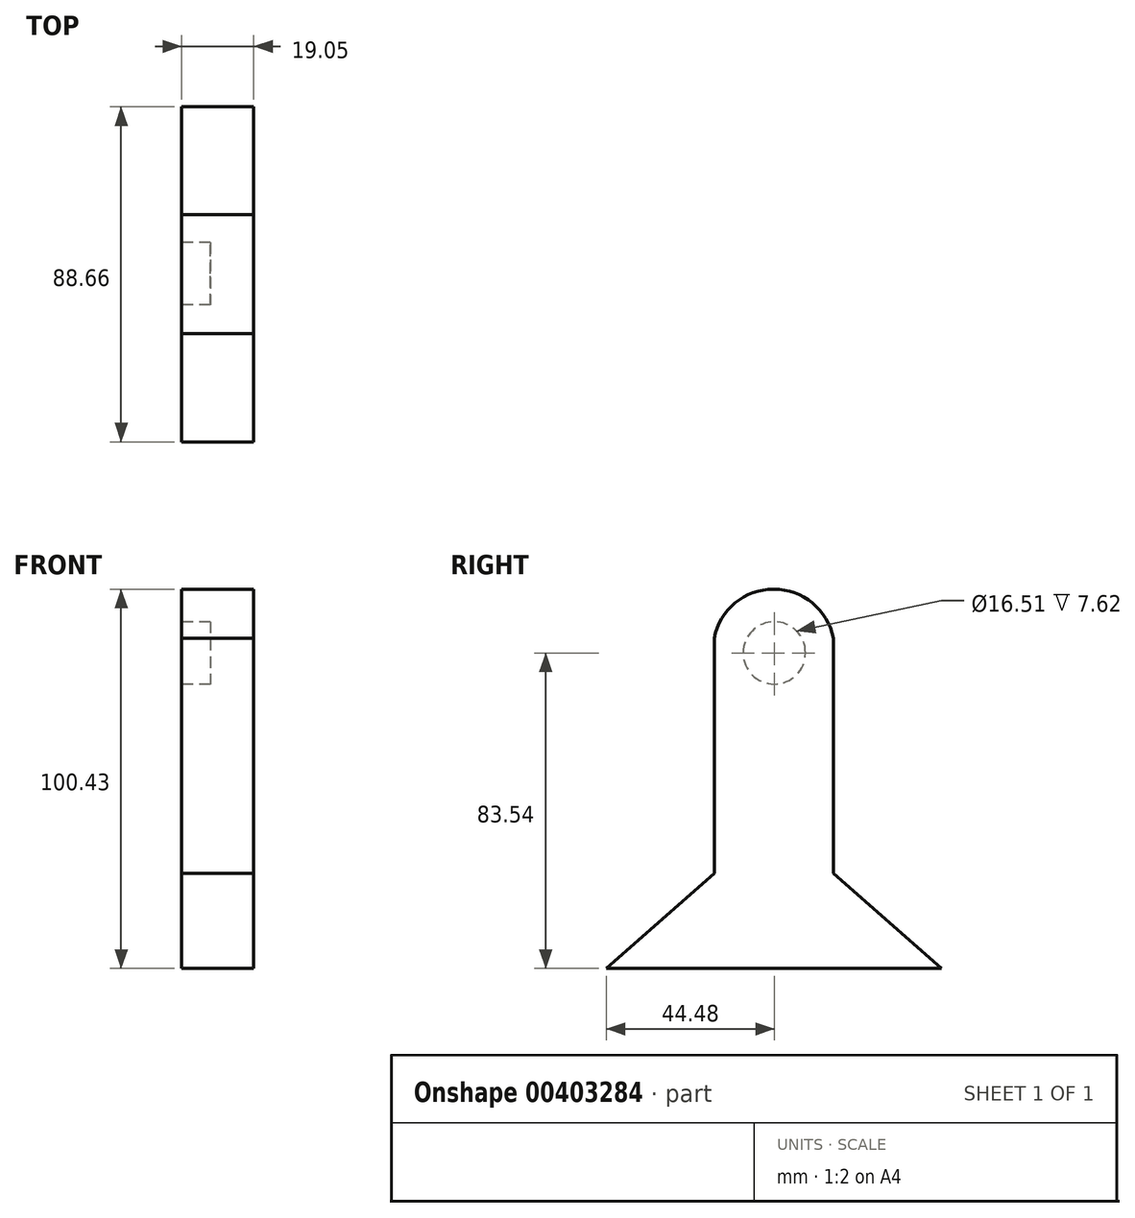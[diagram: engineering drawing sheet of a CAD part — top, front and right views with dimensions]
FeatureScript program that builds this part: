
annotation { "Feature Type Name" : "Feature", "Feature Type Description" : "" }
export const myFeature = defineFeature(function(context is Context, id is Id, definition is map)
    precondition{}
    {
        {
            var Q0;
            Q0=qCreatedBy(makeId("Right.planeOp"),FACE);
            var sketch = newSketch(context, id + "F0", { "sketchPlane" : qUnion([Q0])});
            skLineSegment(sketch, "E0", {"start": v(-15.9, -58.34) * mm, "end": v(-44.48, -83.54) * mm});
            skLineSegment(sketch, "E1.MirrorCS", {"start": v(15.6, -58.34) * mm, "end": v(44.18, -83.54) * mm});
            skLineSegment(sketch, "E2", {"start": v(-44.48, -83.54) * mm, "end": v(44.18, -83.54) * mm});
            skLineSegment(sketch, "E3", {"start": v(-15.9, -58.34) * mm, "end": v(-15.9, 3.9) * mm});
            skLineSegment(sketch, "E4", {"start": v(15.6, -58.34) * mm, "end": v(15.6, 3.9) * mm});
            skArc(sketch, "E5", {"start": v(15.6, 3.9) * mm, "mid": v(-0.15, 16.89) * mm, "end": v(-15.9, 3.9) * mm});
            skSolve(sketch);
        }
        {
            var Q0;
            Q0=makeQuery(id+"F0.imprint","IMPRINT",FACE,{"disambiguationData":[TD([[makeQuery(id+"F0.imprint","IMPRINT",EDGE,{"derivedFrom":sQuery(id+"F0.wireOp",EDGE,"E0")}),1.0]])]});
            extrude(context, id + "F1", {"entities" : qUnion([Q0]), "depth" : 19.05 * mm});
        }
        {
            var Q0;
            Q0=makeQuery(id+"F1.opExtrude","CAP_FACE",FACE,{"disambiguationData":[OSD([sQuery(id+"F0.wireOp",EDGE,"E0"),sQuery(id+"F0.wireOp",EDGE,"E1.MirrorCS"),sQuery(id+"F0.wireOp",EDGE,"E2"),sQuery(id+"F0.wireOp",EDGE,"E3"),sQuery(id+"F0.wireOp",EDGE,"E4"),sQuery(id+"F0.wireOp",EDGE,"E5")])],"isStart":true});
            var sketch = newSketch(context, id + "F2", { "sketchPlane" : qUnion([Q0])});
            skPoint(sketch, "E6.orphan", {"position": v(0, -3.25) * mm});
            skCircle(sketch, "E7", {"center": v(0, 0) * mm, "radius": 8.26 * mm});
            skSolve(sketch);
        }
        {
            var Q0;
            Q0 = qSketchRegion(id + "F2", true);
            extrude(context, id + "F3", {"entities" : qUnion([Q0]), "operationType" : NewBodyOperationType.REMOVE, "oppositeDirection" : true, "depth" : 7.62 * mm});
        }
    });
